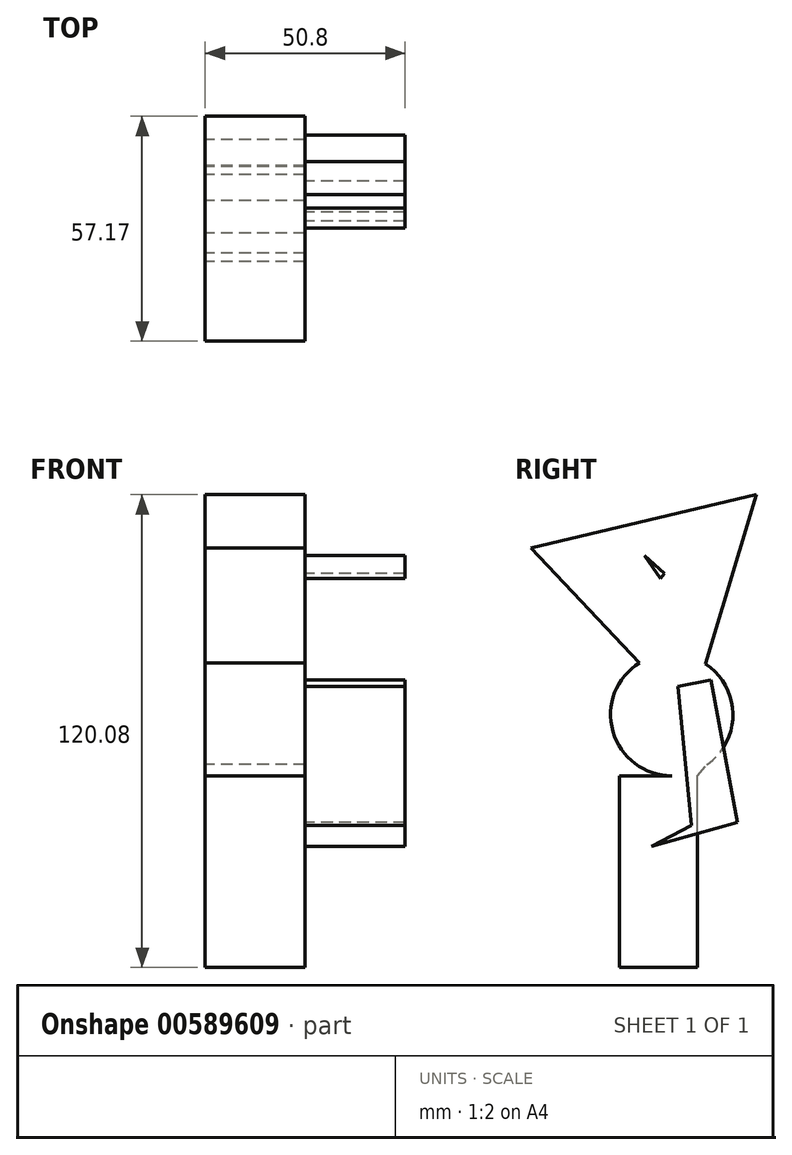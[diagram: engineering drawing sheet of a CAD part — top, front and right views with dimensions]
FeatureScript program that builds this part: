
annotation { "Feature Type Name" : "Feature", "Feature Type Description" : "" }
export const myFeature = defineFeature(function(context is Context, id is Id, definition is map)
    precondition{}
    {
        {
            var Q0;
            Q0=qCreatedBy(makeId("Right.planeOp"),FACE);
            var sketch = newSketch(context, id + "F0", { "sketchPlane" : qUnion([Q0])});
            skLineSegment(sketch, "E0.bottom", {"start": v(-13.29, -64.2) * mm, "end": v(6.57, -64.2) * mm});
            skLineSegment(sketch, "E0.top", {"start": v(-13.29, -15.53) * mm, "end": v(6.57, -15.53) * mm});
            skLineSegment(sketch, "E0.left", {"start": v(-13.29, -64.2) * mm, "end": v(-13.29, -15.53) * mm});
            skLineSegment(sketch, "E0.right", {"start": v(6.57, -64.2) * mm, "end": v(6.57, -15.53) * mm});
            skCircle(sketch, "E1", {"center": v(0, 0) * mm, "radius": 15.53 * mm});
            skCircle(sketch, "E2.cCircle", {"center": v(-3.22, 32.6) * mm, "radius": 16.96 * mm, "construction": true});
            skLineSegment(sketch, "E2.0", {"start": v(-35.72, 42.31) * mm, "end": v(21.45, 55.88) * mm});
            skLineSegment(sketch, "E2.1", {"start": v(21.45, 55.88) * mm, "end": v(4.62, -0.42) * mm});
            skLineSegment(sketch, "E2.2", {"start": v(4.62, -0.42) * mm, "end": v(-35.72, 42.31) * mm});
            skPoint(sketch, "E2.0.midPoint", {"position": v(-7.13, 49.1) * mm});
            skLineSegment(sketch, "E3", {"start": v(0, -15.53) * mm, "end": v(54.7, -51.06) * mm});
            skLineSegment(sketch, "E4", {"start": v(-13.29, -15.53) * mm, "end": v(-68.68, 57.49) * mm});
            skLineSegment(sketch, "E5", {"start": v(6.57, -15.53) * mm, "end": v(65.32, 54.7) * mm});
            skLineSegment(sketch, "E6", {"start": v(-8.53, -43.5) * mm, "end": v(-45.46, -71.76) * mm});
            skLineSegment(sketch, "E7", {"start": v(-13.29, 37.35) * mm, "end": v(-13.29, 27) * mm});
            skSolve(sketch);
        }
        {
            var Q0;
            Q0 = qSketchRegion(id + "F0", true);
            extrude(context, id + "F1", {"entities" : qUnion([Q0]), "depth" : 25.4 * mm, "offsetDistance" : 25.4 * mm});
        }
        {
            var Q0;
            Q0=makeQuery(id+"F1.opExtrude","CAP_FACE",FACE,{"disambiguationData":[OSD([sQuery(id+"F0.wireOp",EDGE,"E0.bottom"),sQuery(id+"F0.wireOp",EDGE,"E0.top"),sQuery(id+"F0.wireOp",EDGE,"E0.left"),sQuery(id+"F0.wireOp",EDGE,"E0.right"),sQuery(id+"F0.wireOp",EDGE,"E1"),sQuery(id+"F0.wireOp",EDGE,"E2.0"),sQuery(id+"F0.wireOp",EDGE,"E2.1"),sQuery(id+"F0.wireOp",EDGE,"E2.2"),sQuery(id+"F0.wireOp",EDGE,"E5")])],"isStart":false});
            var sketch = newSketch(context, id + "F2", { "sketchPlane" : qUnion([Q0])});
            skLineSegment(sketch, "E8", {"start": v(15.22, 3.06) * mm, "end": v(49.94, 35.95) * mm});
            skLineSegment(sketch, "E9", {"start": v(49.94, 35.95) * mm, "end": v(57.66, 27.8) * mm});
            skLineSegment(sketch, "E10", {"start": v(57.66, 25.6) * mm, "end": v(19.44, -3.5) * mm});
            skLineSegment(sketch, "E11", {"start": v(15.22, 3.06) * mm, "end": v(19.44, -3.5) * mm});
            skLineSegment(sketch, "E12", {"start": v(-14.93, -4.27) * mm, "end": v(-51.34, 25.32) * mm});
            skLineSegment(sketch, "E13", {"start": v(-54.97, 20) * mm, "end": v(-60.85, 7.13) * mm});
            skLineSegment(sketch, "E14", {"start": v(-54.97, 20) * mm, "end": v(-50, 30.9) * mm});
            skLineSegment(sketch, "E15", {"start": v(-59.62, 9.81) * mm, "end": v(-23.92, -12.69) * mm});
            skLineSegment(sketch, "E16", {"start": v(-23.92, -12.17) * mm, "end": v(1.54, 0.42) * mm});
            skLineSegment(sketch, "E17", {"start": v(3.22, 42.31) * mm, "end": v(-8.22, 27.8) * mm});
            skLineSegment(sketch, "E18", {"start": v(-8.22, 42.31) * mm, "end": v(8.6, 17.76) * mm});
            skLineSegment(sketch, "E19", {"start": v(1.54, 7.13) * mm, "end": v(6.57, -44.9) * mm});
            skLineSegment(sketch, "E20", {"start": v(-35.72, -26.72) * mm, "end": v(49.94, -3.5) * mm});
            skLineSegment(sketch, "E21", {"start": v(6.57, -44.9) * mm, "end": v(19.44, -43.66) * mm});
            skLineSegment(sketch, "E22", {"start": v(19.72, -43.78) * mm, "end": v(9.93, 8.81) * mm});
            skLineSegment(sketch, "E23", {"start": v(1.54, 7.13) * mm, "end": v(9.93, 8.81) * mm});
            skLineSegment(sketch, "E24", {"start": v(-35.72, -26.72) * mm, "end": v(-31.75, -35.67) * mm});
            skLineSegment(sketch, "E25", {"start": v(-31.75, -35.67) * mm, "end": v(-21.96, -55.53) * mm});
            skLineSegment(sketch, "E26", {"start": v(-21.96, -55.53) * mm, "end": v(60.57, -39.03) * mm});
            skLineSegment(sketch, "E27", {"start": v(60.57, -39.03) * mm, "end": v(67.28, -26.72) * mm});
            skLineSegment(sketch, "E28", {"start": v(67.28, -26.44) * mm, "end": v(39.87, -23.92) * mm});
            skLineSegment(sketch, "E29", {"start": v(39.87, -23.92) * mm, "end": v(65.6, -14.13) * mm});
            skLineSegment(sketch, "E30", {"start": v(63.92, -14.13) * mm, "end": v(-5.18, -33.43) * mm});
            skLineSegment(sketch, "E31", {"start": v(-5.18, -33.43) * mm, "end": v(51.9, -3.5) * mm});
            skLineSegment(sketch, "E32", {"start": v(-31.75, 63.36) * mm, "end": v(15.22, 20) * mm});
            skLineSegment(sketch, "E33", {"start": v(-31.75, 63.36) * mm, "end": v(43.78, 70.36) * mm});
            skLineSegment(sketch, "E34", {"start": v(43.78, 70.36) * mm, "end": v(49.38, 52.73) * mm});
            skLineSegment(sketch, "E35", {"start": v(49.38, 52.73) * mm, "end": v(30.07, 55.81) * mm});
            skLineSegment(sketch, "E36", {"start": v(30.07, 55.81) * mm, "end": v(28.67, 37.07) * mm});
            skLineSegment(sketch, "E37", {"start": v(28.67, 36.79) * mm, "end": v(23.36, 33.43) * mm});
            skLineSegment(sketch, "E38", {"start": v(23.36, 33.43) * mm, "end": v(19.44, 42.31) * mm});
            skLineSegment(sketch, "E39", {"start": v(18.04, 42.38) * mm, "end": v(15.22, 20) * mm});
            skSolve(sketch);
        }
        {
            var Q0;
            Q0 = qSketchRegion(id + "F2", true);
            extrude(context, id + "F3", {"entities" : qUnion([Q0]), "operationType" : NewBodyOperationType.ADD, "depth" : 25.4 * mm, "offsetDistance" : 25.4 * mm});
        }
    });
